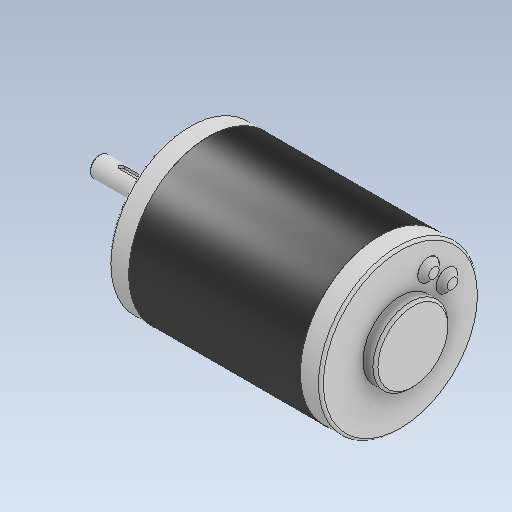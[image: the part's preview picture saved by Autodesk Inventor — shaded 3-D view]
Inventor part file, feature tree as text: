
AUTODESK INVENTOR PART (.ipt)
format: ipt  version: 2020 (Build 240168000, 168)  size: 185,856 bytes
history: native  units: in
note: dims shown in document units (in); Inventor stores cm internally (conversion verified against a paired STEP export)
features: chamfer x1
ambient origin geometry x8: Origin, YZ Plane, XZ Plane, XY Plane, X Axis, Y Axis, Z Axis, Center Point
bodies: Solid1 (feature_tree)
feature tree (1):
  chamfer  "Chamfer3"  [1 undecoded]
note: 1 required parameter value undecoded (feature->parameter linkage not recoverable at this tier; creation-order binding heuristic only, values carry confidence <= 0.55)
